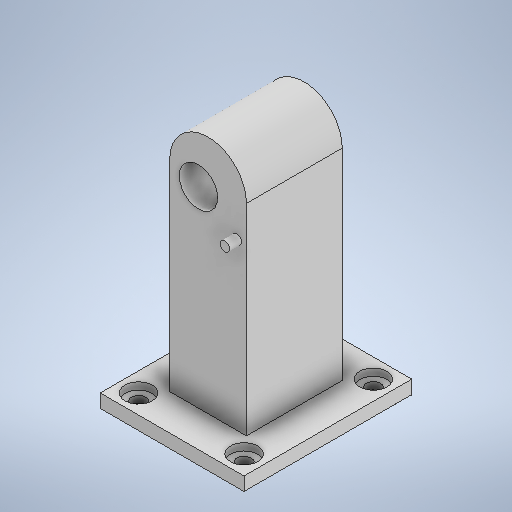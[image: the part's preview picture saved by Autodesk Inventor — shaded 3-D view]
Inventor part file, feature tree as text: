
AUTODESK INVENTOR PART (.ipt)
format: ipt  version: 2025 (Build 290162000, 162)  size: 674,816 bytes
history: native  units: mm
features: extrude x8, sketch x5, other x3, fillet x2
ambient origin geometry x8: Origin, YZ Plane, XZ Plane, XY Plane, X Axis, Y Axis, Z Axis, Center Point
bodies: Body1 (feature_tree)
feature tree (18):
  other  "ソリッド1"
  extrude  "本体"  Depth=16.0mm
  extrude  "ねじ穴"  Depth=20.0mm
  extrude  "接合部"  Depth=50.0mm TaperAngle=0.0deg
  extrude  "ナット穴"  Depth=10.0mm
  fillet  "フィレット1"  Radius=12.0mm
  extrude  "足場"  Depth=2.9mm
  extrude  "ストッパー"  Depth=8.0mm
  extrude  "押し出し7"  Depth=8.0mm TaperAngle=0.0deg
  extrude  "ネジ溝"  Depth=2.7mm
  fillet  "フィレット2"  Radius=5.4mm
  other  "ねじ穴スケッチ"
  other  "接合部スケッチ"
  sketch  "スケッチ4"
  sketch  "スケッチ5"
  sketch  "スケッチ6"
  sketch  "スケッチ7"
  sketch  "スケッチ8"
